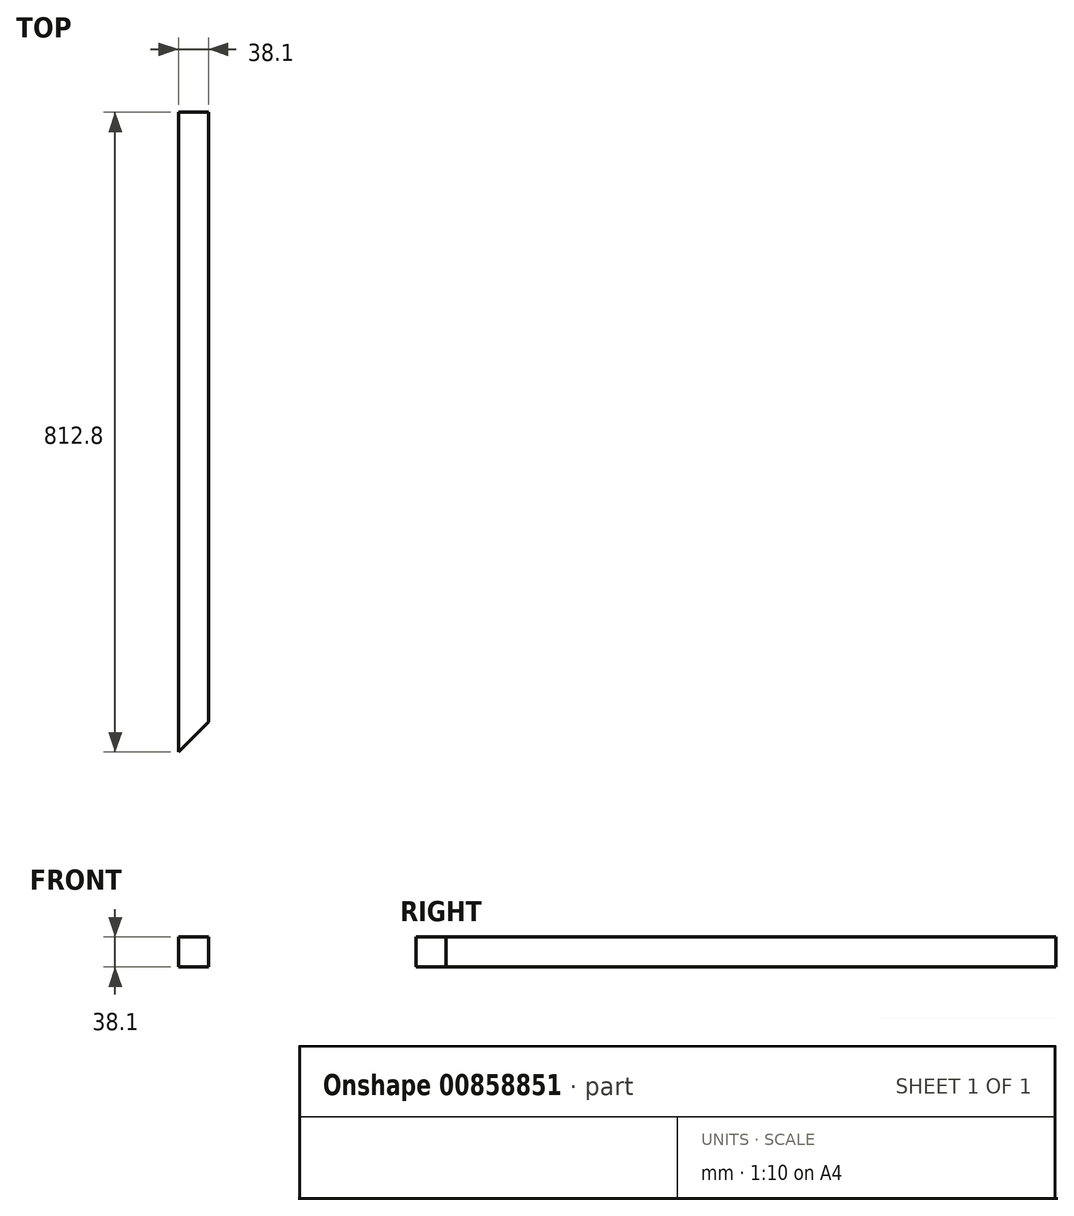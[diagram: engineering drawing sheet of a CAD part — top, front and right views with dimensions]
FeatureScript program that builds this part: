
annotation { "Feature Type Name" : "Feature", "Feature Type Description" : "" }
export const myFeature = defineFeature(function(context is Context, id is Id, definition is map)
    precondition{}
    {
        {
            var Q0;
            Q0=qCreatedBy(makeId("Front.planeOp"),FACE);
            var sketch = newSketch(context, id + "F0", { "sketchPlane" : qUnion([Q0])});
            skLineSegment(sketch, "E0.bottom", {"start": v(-72.89, 70.43) * mm, "end": v(-34.79, 70.43) * mm});
            skLineSegment(sketch, "E0.top", {"start": v(-72.89, 32.33) * mm, "end": v(-34.79, 32.33) * mm});
            skLineSegment(sketch, "E0.left", {"start": v(-72.89, 70.43) * mm, "end": v(-72.89, 32.33) * mm});
            skLineSegment(sketch, "E0.right", {"start": v(-34.79, 70.43) * mm, "end": v(-34.79, 32.33) * mm});
            skSolve(sketch);
        }
        {
            var Q0;
            Q0=makeQuery(id+"F0.imprint","IMPRINT",FACE,{"disambiguationData":[TD([[makeQuery(id+"F0.imprint","IMPRINT",EDGE,{"derivedFrom":sQuery(id+"F0.wireOp",EDGE,"E0.bottom")}),-1.0]])]});
            extrude(context, id + "F1", {"entities" : qUnion([Q0]), "depth" : 863.6 * mm, "offsetDistance" : 25.4 * mm});
        }
        {
            var Q0;
            Q0=makeQuery(id+"F1.opExtrude","SWEPT_FACE",FACE,{"disambiguationData":[OSD([sQuery(id+"F0.wireOp",EDGE,"E0.bottom")])]});
            var sketch = newSketch(context, id + "F2", { "sketchPlane" : qUnion([Q0])});
            skLineSegment(sketch, "E1.bottom", {"start": v(-72.89, -863.6) * mm, "end": v(-34.79, -863.6) * mm});
            skLineSegment(sketch, "E1.top", {"start": v(-72.89, -825.5) * mm, "end": v(-34.79, -825.5) * mm});
            skLineSegment(sketch, "E1.left", {"start": v(-72.89, -863.6) * mm, "end": v(-72.89, -825.5) * mm});
            skLineSegment(sketch, "E1.right", {"start": v(-34.79, -863.6) * mm, "end": v(-34.79, -825.5) * mm});
            skLineSegment(sketch, "E2", {"start": v(-72.89, -863.6) * mm, "end": v(-34.79, -825.5) * mm});
            skLineSegment(sketch, "E3", {"start": v(-34.79, -825.5) * mm, "end": v(-34.79, -863.6) * mm});
            skSolve(sketch);
        }
        {
            var Q0;
            Q0=makeQuery(id+"F2.imprint","IMPRINT",FACE,{"disambiguationData":[TD([[makeQuery(id+"F2.imprint","IMPRINT",EDGE,{"derivedFrom":sQuery(id+"F2.wireOp",EDGE,"E1.bottom")}),1.0]])]});
            extrude(context, id + "F3", {"entities" : qUnion([Q0]), "operationType" : NewBodyOperationType.REMOVE, "oppositeDirection" : true, "depth" : 50.8 * mm, "offsetDistance" : 25.4 * mm});
        }
        {
            var Q0;
            Q0=makeQuery(id+"F1.opExtrude","CAP_FACE",FACE,{"disambiguationData":[OSD([sQuery(id+"F0.wireOp",EDGE,"E0.bottom"),sQuery(id+"F0.wireOp",EDGE,"E0.top"),sQuery(id+"F0.wireOp",EDGE,"E0.left"),sQuery(id+"F0.wireOp",EDGE,"E0.right")])],"isStart":true});
            extrude(context, id + "F4", {"entities" : qUnion([Q0]), "operationType" : NewBodyOperationType.REMOVE, "oppositeDirection" : true, "depth" : 50.8 * mm, "offsetDistance" : 25.4 * mm});
        }
    });
